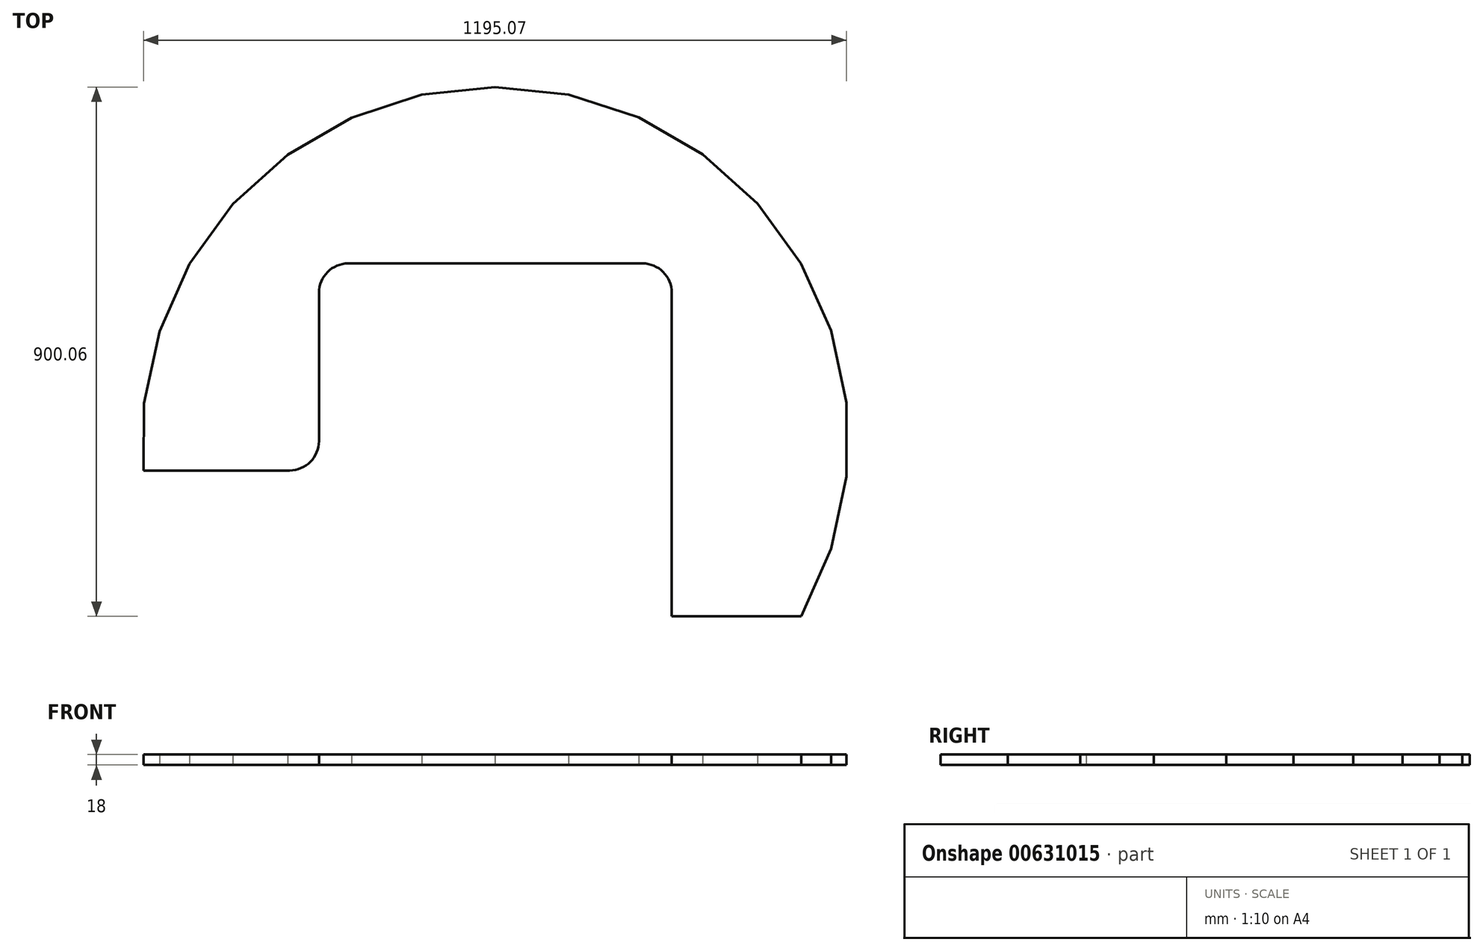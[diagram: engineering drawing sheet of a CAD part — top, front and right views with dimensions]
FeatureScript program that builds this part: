
annotation { "Feature Type Name" : "Feature", "Feature Type Description" : "" }
export const myFeature = defineFeature(function(context is Context, id is Id, definition is map)
    precondition{}
    {
        {
            var Q0;
            Q0=qCreatedBy(makeId("Top.planeOp"),FACE);
            var sketch = newSketch(context, id + "F0", { "sketchPlane" : qUnion([Q0])});
            skLineSegment(sketch, "E0.top", {"start": v(-250, 300) * mm, "end": v(250, 300) * mm});
            skLineSegment(sketch, "E0.left", {"start": v(-300, -2.1) * mm, "end": v(-300, 250) * mm});
            skLineSegment(sketch, "E0.right", {"start": v(300, -300) * mm, "end": v(300, 250) * mm});
            skPoint(sketch, "E0.middle", {"position": v(0, 0) * mm});
            skLineSegment(sketch, "E1", {"start": v(-598.32, -52.1) * mm, "end": v(-348.32, -52.1) * mm});
            skPoint(sketch, "E2.end.orphan", {"position": v(-300, -300) * mm});
            skLineSegment(sketch, "E3.13", {"start": v(-597.25, 61.9) * mm, "end": v(-571.16, 184.66) * mm});
            skLineSegment(sketch, "E3.14", {"start": v(-571.16, 184.66) * mm, "end": v(-520.11, 299.31) * mm});
            skLineSegment(sketch, "E3.15", {"start": v(-520.11, 299.31) * mm, "end": v(-446.48, 400.94) * mm});
            skLineSegment(sketch, "E3.16", {"start": v(-446.48, 400.94) * mm, "end": v(-353.32, 485.03) * mm});
            skLineSegment(sketch, "E3.17", {"start": v(-353.32, 485.03) * mm, "end": v(-244.7, 547.91) * mm});
            skLineSegment(sketch, "E3.18", {"start": v(-244.7, 547.91) * mm, "end": v(-125.4, 586.82) * mm});
            skLineSegment(sketch, "E3.19", {"start": v(-125.4, 586.82) * mm, "end": v(-0.6, 600.06) * mm});
            skLineSegment(sketch, "E3.20", {"start": v(-0.6, 600.06) * mm, "end": v(124.23, 587.06) * mm});
            skLineSegment(sketch, "E3.21", {"start": v(124.23, 587.06) * mm, "end": v(243.62, 548.37) * mm});
            skLineSegment(sketch, "E3.22", {"start": v(243.62, 548.37) * mm, "end": v(352.35, 485.7) * mm});
            skLineSegment(sketch, "E3.23", {"start": v(352.35, 485.7) * mm, "end": v(445.67, 401.78) * mm});
            skLineSegment(sketch, "E3.24", {"start": v(445.67, 401.78) * mm, "end": v(519.49, 300.29) * mm});
            skLineSegment(sketch, "E3.25", {"start": v(519.49, 300.29) * mm, "end": v(570.58, 185.66) * mm});
            skLineSegment(sketch, "E3.26", {"start": v(570.58, 185.66) * mm, "end": v(596.71, 62.9) * mm});
            skLineSegment(sketch, "E3.27", {"start": v(596.71, 62.9) * mm, "end": v(596.75, -62.6) * mm});
            skLineSegment(sketch, "E3.28", {"start": v(596.75, -62.6) * mm, "end": v(570.66, -185.35) * mm});
            skLineSegment(sketch, "E4", {"start": v(-597.25, 61.9) * mm, "end": v(-598.32, -52.1) * mm});
            skPoint(sketch, "E5.visualSharp", {"position": v(-300, 300) * mm});
            skArc(sketch, "E5.filletArc", {"start": v(-250, 300) * mm, "mid": v(-285.36, 285.36) * mm, "end": v(-300, 250) * mm});
            skPoint(sketch, "E6.visualSharp", {"position": v(-300, -52.1) * mm});
            skPoint(sketch, "E7.visualSharp", {"position": v(300, 300) * mm});
            skArc(sketch, "E7.filletArc", {"start": v(300, 250) * mm, "mid": v(285.36, 285.36) * mm, "end": v(250, 300) * mm});
            skLineSegment(sketch, "E8", {"start": v(300, -300) * mm, "end": v(520, -300) * mm});
            skLineSegment(sketch, "E9", {"start": v(570.66, -185.35) * mm, "end": v(520, -300) * mm});
            skLineSegment(sketch, "E10", {"start": v(-350, -52.1) * mm, "end": v(-348.32, -52.1) * mm});
            skLineSegment(sketch, "E11", {"start": v(-300, -2.1) * mm, "end": v(-300, -2.1) * mm});
            skArc(sketch, "E12.filletArc", {"start": v(-350, -52.1) * mm, "mid": v(-314.64, -37.45) * mm, "end": v(-300, -2.1) * mm});
            skLineSegment(sketch, "E13", {"start": v(-300, 250) * mm, "end": v(-542.07, 250) * mm});
            skLineSegment(sketch, "E14", {"start": v(250, 300) * mm, "end": v(250, 544.7) * mm});
            skLineSegment(sketch, "E15", {"start": v(300, 250) * mm, "end": v(541.9, 250) * mm});
            skLineSegment(sketch, "E16", {"start": v(-250, 300) * mm, "end": v(-250, 544.85) * mm});
            skSolve(sketch);
        }
        {
            var Q0;
            Q0 = qSketchRegion(id + "F0", true);
            extrude(context, id + "F1", {"entities" : qUnion([Q0]), "depth" : 18 * mm, "offsetDistance" : 25 * mm});
        }
    });
